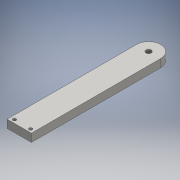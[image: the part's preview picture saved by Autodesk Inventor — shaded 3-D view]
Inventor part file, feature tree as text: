
AUTODESK INVENTOR PART (.ipt)
format: ipt  version: 2016 SP1 (Build 200210100, 210)  size: 105,984 bytes
history: native  units: mm
features: extrude x1, sketch x1
ambient origin geometry x8: Origin, YZ Plane, XZ Plane, XY Plane, X Axis, Y Axis, Z Axis, Center Point
bodies: Solid1 (feature_tree)
feature tree (2):
  extrude  "Extrusion1"  Depth=15.0mm
  sketch  "Sketch1"  dims[d0=125.0mm d1=30.0mm d2=62.5mm d3=15.0mm d4=6.4mm d5=15.0mm d6=10.0mm d7=4.0mm d8=4.0mm d9=5.0mm d10=4.0mm d11=4.0mm d12=5.0mm d13=10.0mm d14=0.0mm d17=160.0mm]
